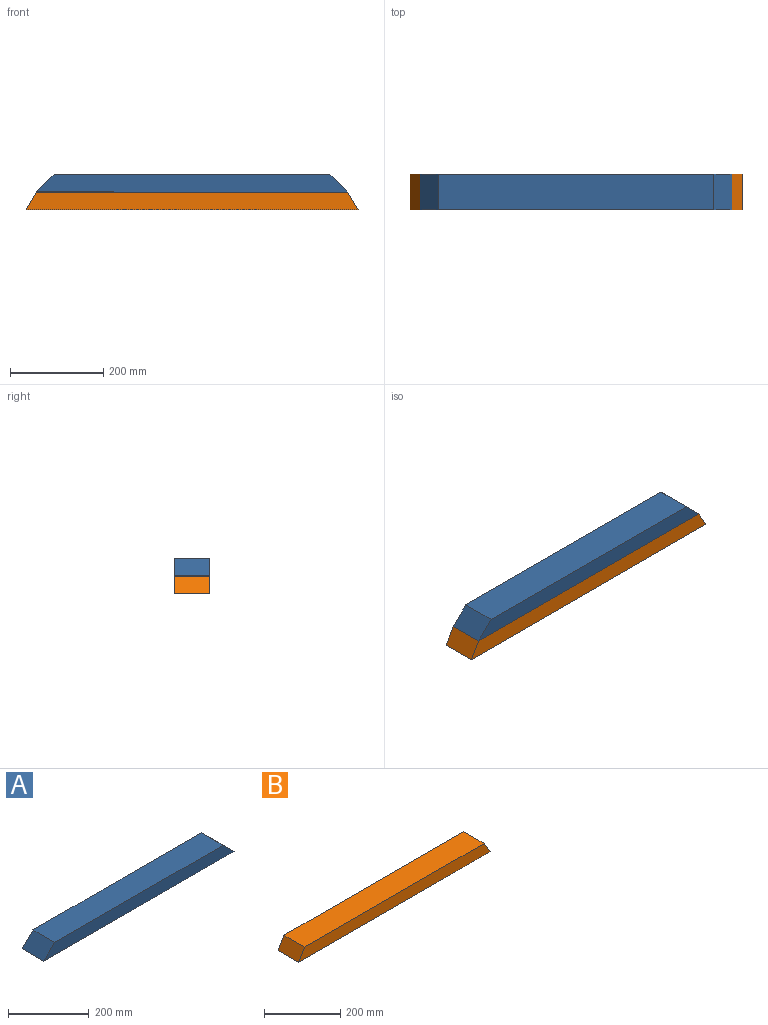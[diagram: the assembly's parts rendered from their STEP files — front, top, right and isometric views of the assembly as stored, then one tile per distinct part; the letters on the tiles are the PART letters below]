
ASSEMBLY  parts=2 mates=1
PART A: 6 faces, bbox 667.2x76.2x38.1 mm
  f0: plane 591.01x76.2mm, normal (0,0,1), area 45034.7mm2, adj f1,f3,f4,f5
  f1: plane 76.2x38.1mm, normal (-0.71,0,0.71), area 4105.8mm2, adj f0,f2,f4,f5
  f2: plane 667.21x76.2mm, normal (0,0,-1), area 50841.2mm2, adj f1,f3,f4,f5
  f3: plane 76.2x38.1mm, normal (0.71,0,0.71), area 4105.8mm2, adj f0,f2,f4,f5
  f4: plane 667.21x38.1mm, normal (0,1,0), area 23969mm2, adj f0,f1,f2,f3
  f5: plane 667.21x38.1mm, normal (0,-1,0), area 23969mm2, adj f0,f1,f2,f3
PART B: 6 faces, bbox 711.2x76.2x38.1 mm
  f0: plane 76.2x38.1mm, normal (0.87,0,0.5), area 3352.3mm2, adj f1,f3,f4,f5
  f1: plane 667.21x76.2mm, normal (0,0,1), area 50841.1mm2, adj f0,f2,f4,f5
  f2: plane 76.2x38.1mm, normal (-0.87,0,0.5), area 3352.3mm2, adj f1,f3,f4,f5
  f3: plane 711.2x76.2mm, normal (0,0,-1), area 54193.4mm2, adj f0,f2,f4,f5
  f4: plane 711.2x38.1mm, normal (0,1,0), area 26258.6mm2, adj f0,f1,f2,f3
  f5: plane 711.2x38.1mm, normal (0,-1,0), area 26258.6mm2, adj f0,f1,f2,f3
PLACE A t=(0,0,38.1)mm
PLACE B at identity
MATE planar A.f2 <-> B.f1  axis (0,0,-1) through (0,38.1,38.1)mm
